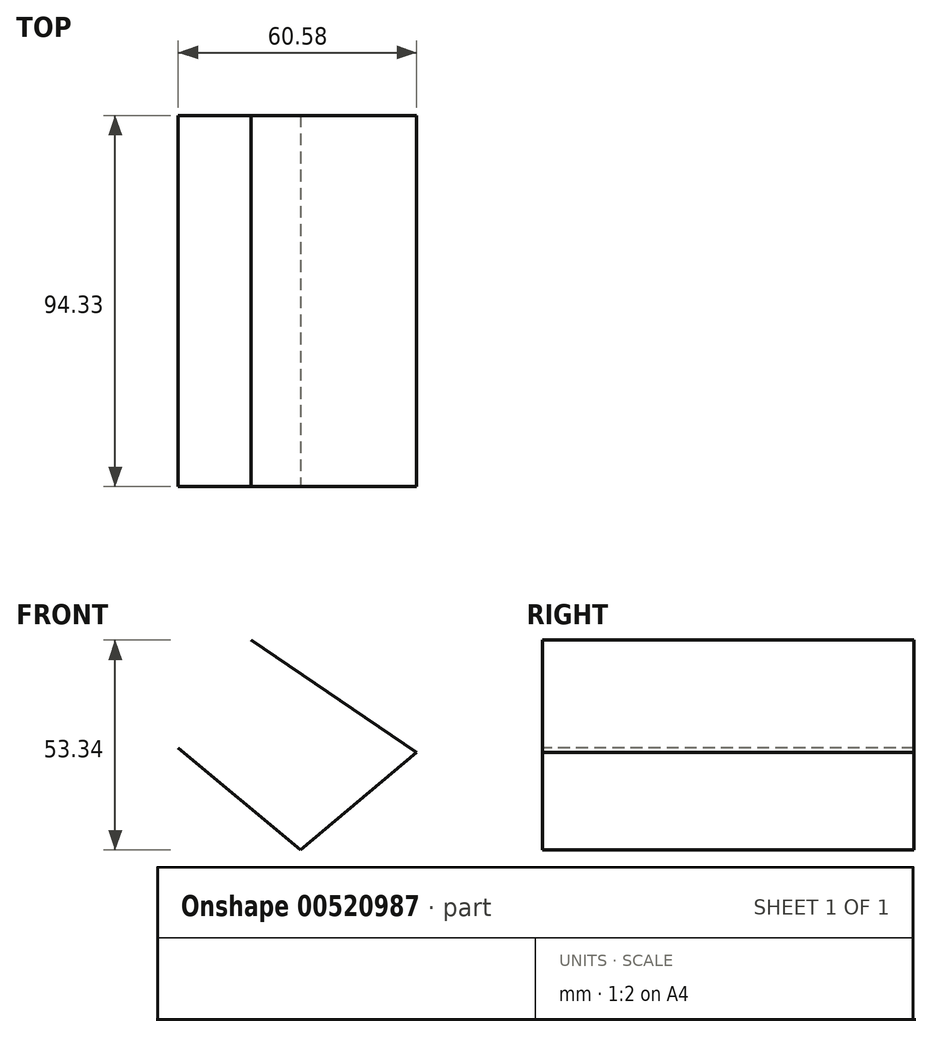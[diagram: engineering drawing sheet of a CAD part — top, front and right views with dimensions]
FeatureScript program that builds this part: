
annotation { "Feature Type Name" : "Feature", "Feature Type Description" : "" }
export const myFeature = defineFeature(function(context is Context, id is Id, definition is map)
    precondition{}
    {
        {
            var Q0;
            Q0=qCreatedBy(makeId("Front.planeOp"),FACE);
            var sketch = newSketch(context, id + "F0", { "sketchPlane" : qUnion([Q0])});
            skLineSegment(sketch, "E0", {"start": v(29.57, 24.81) * mm, "end": v(-12.46, 53.34) * mm});
            skLineSegment(sketch, "E1", {"start": v(-12.46, 53.34) * mm, "end": v(-31, 26.02) * mm, "construction": true});
            skLineSegment(sketch, "E2", {"start": v(-31, 26.02) * mm, "end": v(0, 0) * mm});
            skLineSegment(sketch, "E3", {"start": v(0, 0) * mm, "end": v(29.57, 24.81) * mm});
            skSolve(sketch);
        }
        {
            var Q0;
            Q0=sQuery(id+"F0.wireOp",EDGE,"E3");
            var Q1;
            Q1=sQuery(id+"F0.wireOp",EDGE,"E0");
            var Q2;
            Q2=sQuery(id+"F0.wireOp",EDGE,"E2");
            extrude(context, id + "F1", {"bodyType" : ToolBodyType.SURFACE, "surfaceEntities" : qUnion([Q0, Q1, Q2]), "depth" : 94.33 * mm, "offsetDistance" : 25.4 * mm});
        }
    });
